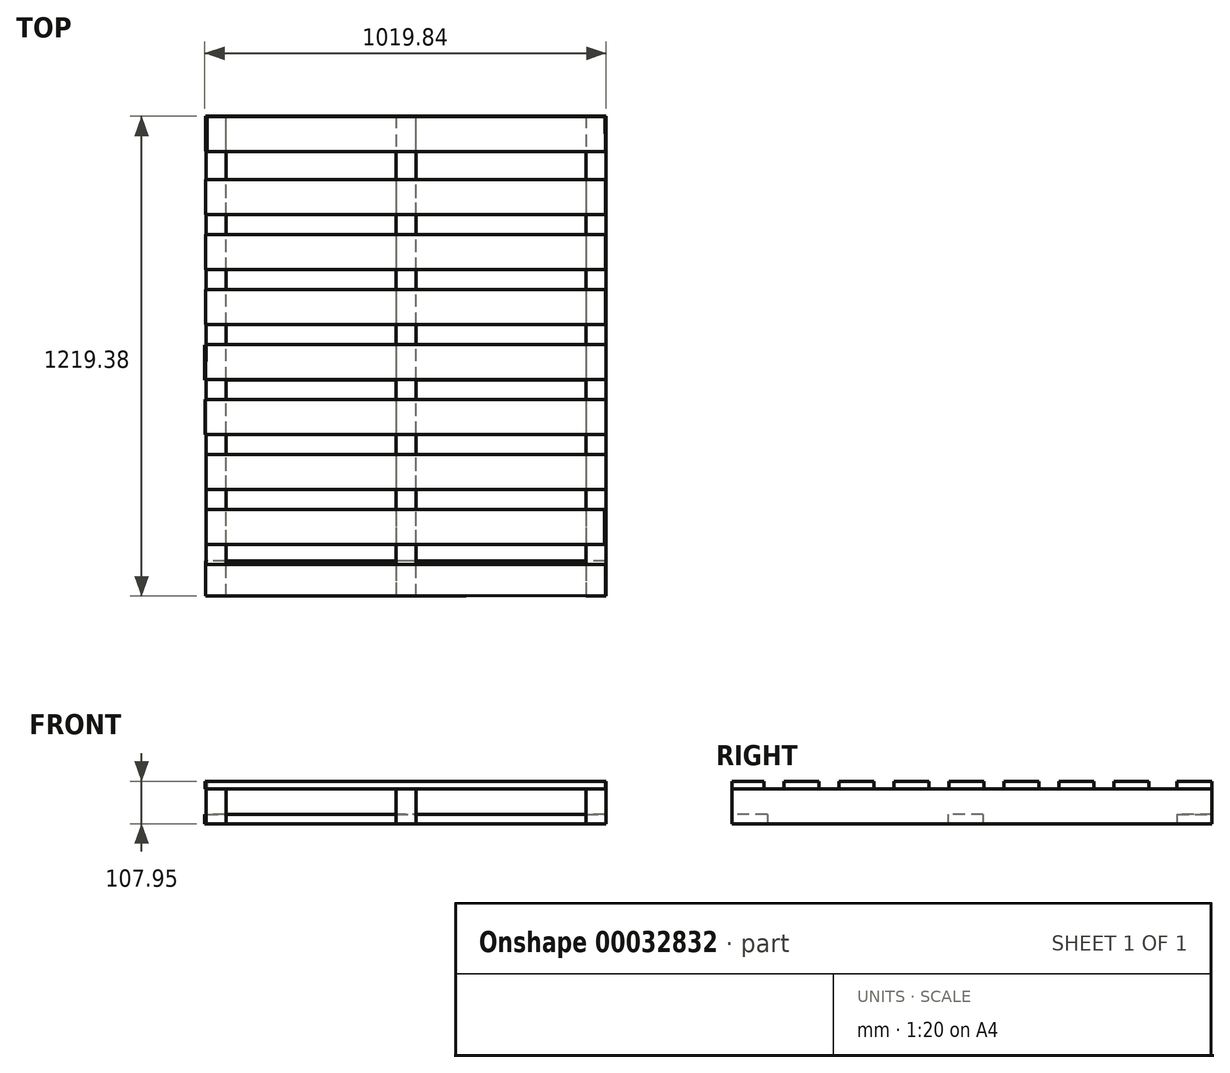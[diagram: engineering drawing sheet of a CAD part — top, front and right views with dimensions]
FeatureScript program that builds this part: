
annotation { "Feature Type Name" : "Feature", "Feature Type Description" : "" }
export const myFeature = defineFeature(function(context is Context, id is Id, definition is map)
    precondition{}
    {
        {
            var Q0;
            Q0=qCreatedBy(makeId("Top.planeOp"),FACE);
            var sketch = newSketch(context, id + "F0", { "sketchPlane" : qUnion([Q0])});
            skLineSegment(sketch, "E0", {"start": v(-409.62, 972.65) * mm, "end": v(-409.62, -246.55) * mm});
            skLineSegment(sketch, "E1", {"start": v(-409.62, -246.55) * mm, "end": v(-358.82, -246.55) * mm});
            skLineSegment(sketch, "E2", {"start": v(-358.82, -246.55) * mm, "end": v(-358.82, 972.65) * mm});
            skLineSegment(sketch, "E3", {"start": v(-358.82, 972.65) * mm, "end": v(-409.62, 972.65) * mm});
            skLineSegment(sketch, "E4", {"start": v(72.98, 972.65) * mm, "end": v(72.98, -246.55) * mm});
            skLineSegment(sketch, "E5", {"start": v(72.98, -246.55) * mm, "end": v(123.78, -246.55) * mm});
            skLineSegment(sketch, "E6", {"start": v(123.78, -246.55) * mm, "end": v(123.78, 972.65) * mm});
            skLineSegment(sketch, "E7", {"start": v(123.78, 972.65) * mm, "end": v(72.98, 972.65) * mm});
            skLineSegment(sketch, "E8", {"start": v(555.58, 972.65) * mm, "end": v(555.58, -246.55) * mm});
            skLineSegment(sketch, "E9", {"start": v(555.58, -246.55) * mm, "end": v(606.38, -246.55) * mm});
            skLineSegment(sketch, "E10", {"start": v(606.38, -246.55) * mm, "end": v(606.38, 972.65) * mm});
            skLineSegment(sketch, "E11", {"start": v(606.38, 972.65) * mm, "end": v(555.58, 972.65) * mm});
            skSolve(sketch);
        }
        {
            var Q0;
            Q0=makeQuery(id+"F0.imprint","IMPRINT",FACE,{"disambiguationData":[TD([[makeQuery(id+"F0.imprint","IMPRINT",EDGE,{"derivedFrom":sQuery(id+"F0.wireOp",EDGE,"E0")}),1.0]])]});
            var Q1;
            Q1=makeQuery(id+"F0.imprint","IMPRINT",FACE,{"disambiguationData":[TD([[makeQuery(id+"F0.imprint","IMPRINT",EDGE,{"derivedFrom":sQuery(id+"F0.wireOp",EDGE,"E4")}),1.0]])]});
            var Q2;
            Q2=makeQuery(id+"F0.imprint","IMPRINT",FACE,{"disambiguationData":[TD([[makeQuery(id+"F0.imprint","IMPRINT",EDGE,{"derivedFrom":sQuery(id+"F0.wireOp",EDGE,"E8")}),1.0]])]});
            extrude(context, id + "F1", {"entities" : qUnion([Q0, Q1, Q2]), "depth" : 88.9 * mm});
        }
        {
            var Q0;
            Q0=makeQuery(id+"F1.opExtrude","CAP_FACE",FACE,{"disambiguationData":[OSD([sQuery(id+"F0.wireOp",EDGE,"E4"),sQuery(id+"F0.wireOp",EDGE,"E5"),sQuery(id+"F0.wireOp",EDGE,"E6"),sQuery(id+"F0.wireOp",EDGE,"E7")])],"isStart":false});
            var sketch = newSketch(context, id + "F2", { "sketchPlane" : qUnion([Q0])});
            skLineSegment(sketch, "E12", {"start": v(-410.98, 812.34) * mm, "end": v(604.56, 812.34) * mm});
            skLineSegment(sketch, "E13", {"start": v(604.56, 812.34) * mm, "end": v(604.56, 723.44) * mm});
            skLineSegment(sketch, "E14", {"start": v(604.56, 723.44) * mm, "end": v(-410.98, 723.44) * mm});
            skLineSegment(sketch, "E15", {"start": v(-410.98, 723.44) * mm, "end": v(-410.98, 812.34) * mm});
            skLineSegment(sketch, "E16", {"start": v(-410.98, 672.64) * mm, "end": v(604.56, 672.64) * mm});
            skLineSegment(sketch, "E17", {"start": v(604.56, 672.64) * mm, "end": v(604.56, 583.74) * mm});
            skLineSegment(sketch, "E18", {"start": v(604.56, 583.74) * mm, "end": v(-410.98, 583.74) * mm});
            skLineSegment(sketch, "E19", {"start": v(-410.98, 583.74) * mm, "end": v(-410.98, 672.64) * mm});
            skLineSegment(sketch, "E20", {"start": v(-410.98, 532.94) * mm, "end": v(604.56, 532.94) * mm});
            skLineSegment(sketch, "E21", {"start": v(604.56, 532.94) * mm, "end": v(604.56, 444.04) * mm});
            skLineSegment(sketch, "E22", {"start": v(604.56, 444.04) * mm, "end": v(-410.98, 444.04) * mm});
            skLineSegment(sketch, "E23", {"start": v(-410.98, 444.04) * mm, "end": v(-410.98, 532.94) * mm});
            skLineSegment(sketch, "E24", {"start": v(-409.91, 393.24) * mm, "end": v(605.66, 393.24) * mm});
            skLineSegment(sketch, "E25", {"start": v(605.66, 393.24) * mm, "end": v(605.66, 304.34) * mm});
            skLineSegment(sketch, "E26", {"start": v(605.66, 304.34) * mm, "end": v(-410.98, 304.34) * mm});
            skLineSegment(sketch, "E27", {"start": v(-410.98, 304.34) * mm, "end": v(-409.91, 393.24) * mm});
            skLineSegment(sketch, "E28", {"start": v(-412.98, 253.54) * mm, "end": v(605.66, 253.54) * mm});
            skLineSegment(sketch, "E29", {"start": v(605.66, 253.54) * mm, "end": v(605.66, 164.64) * mm});
            skLineSegment(sketch, "E30", {"start": v(605.66, 164.64) * mm, "end": v(-412.98, 164.64) * mm});
            skLineSegment(sketch, "E31", {"start": v(-412.98, 164.64) * mm, "end": v(-412.98, 253.54) * mm});
            skLineSegment(sketch, "E32", {"start": v(-410.34, 113.84) * mm, "end": v(605.66, 113.84) * mm});
            skLineSegment(sketch, "E33", {"start": v(605.66, 113.84) * mm, "end": v(605.66, 24.94) * mm});
            skLineSegment(sketch, "E34", {"start": v(605.66, 24.94) * mm, "end": v(-410.34, 24.94) * mm});
            skLineSegment(sketch, "E35", {"start": v(-410.34, 24.94) * mm, "end": v(-410.34, 113.84) * mm});
            skLineSegment(sketch, "E36", {"start": v(-410.34, -25.86) * mm, "end": v(602.28, -25.86) * mm});
            skLineSegment(sketch, "E37", {"start": v(602.28, -25.86) * mm, "end": v(602.28, -114.76) * mm});
            skLineSegment(sketch, "E38", {"start": v(602.28, -114.76) * mm, "end": v(-410.34, -114.76) * mm});
            skLineSegment(sketch, "E39", {"start": v(-410.34, -114.76) * mm, "end": v(-410.34, -25.86) * mm});
            skLineSegment(sketch, "E40", {"start": v(-410.69, -245.09) * mm, "end": v(604.77, -246.55) * mm});
            skLineSegment(sketch, "E41", {"start": v(604.77, -246.55) * mm, "end": v(604.77, -165.56) * mm});
            skLineSegment(sketch, "E42", {"start": v(604.77, -165.56) * mm, "end": v(-410.69, -165.56) * mm});
            skLineSegment(sketch, "E43", {"start": v(-410.69, -165.56) * mm, "end": v(-410.69, -245.09) * mm});
            skLineSegment(sketch, "E44", {"start": v(604.77, 883.24) * mm, "end": v(604.53, 883.24) * mm});
            skLineSegment(sketch, "E45", {"start": v(-407.36, 972.14) * mm, "end": v(603.42, 972.14) * mm});
            skLineSegment(sketch, "E46", {"start": v(603.42, 972.14) * mm, "end": v(604.77, 883.24) * mm});
            skLineSegment(sketch, "E47", {"start": v(-407.36, 972.14) * mm, "end": v(-407.36, 883.24) * mm});
            skLineSegment(sketch, "E48", {"start": v(-407.36, 883.24) * mm, "end": v(604.77, 883.24) * mm});
            skSolve(sketch);
        }
        {
            var Q0;
            Q0 = qSketchRegion(id + "F2", true);
            extrude(context, id + "F3", {"entities" : qUnion([Q0]), "depth" : 19.05 * mm});
        }
        {
            var Q0;
            Q0=qCreatedBy(makeId("Top.planeOp"),FACE);
            var sketch = newSketch(context, id + "F4", { "sketchPlane" : qUnion([Q0])});
            skLineSegment(sketch, "E49", {"start": v(-411.07, -246.04) * mm, "end": v(604.47, -246.04) * mm});
            skLineSegment(sketch, "E50", {"start": v(604.47, -246.04) * mm, "end": v(604.47, -157.14) * mm});
            skLineSegment(sketch, "E51", {"start": v(604.47, -157.14) * mm, "end": v(-411.07, -157.14) * mm});
            skLineSegment(sketch, "E52", {"start": v(-411.07, -157.14) * mm, "end": v(-411.07, -246.04) * mm});
            skLineSegment(sketch, "E53", {"start": v(-411.07, 883.93) * mm, "end": v(-411.07, 972.83) * mm});
            skLineSegment(sketch, "E54", {"start": v(-411.07, 972.83) * mm, "end": v(604.47, 972.83) * mm});
            skLineSegment(sketch, "E55", {"start": v(604.47, 972.83) * mm, "end": v(604.47, 883.93) * mm});
            skLineSegment(sketch, "E56", {"start": v(604.47, 883.93) * mm, "end": v(-411.07, 883.93) * mm});
            skLineSegment(sketch, "E57", {"start": v(-413.46, 302.26) * mm, "end": v(604.47, 302.26) * mm});
            skLineSegment(sketch, "E58", {"start": v(604.47, 302.26) * mm, "end": v(604.47, 391.16) * mm});
            skLineSegment(sketch, "E59", {"start": v(604.47, 391.16) * mm, "end": v(-413.46, 391.16) * mm});
            skLineSegment(sketch, "E60", {"start": v(-413.46, 391.16) * mm, "end": v(-413.46, 302.26) * mm});
            skLineSegment(sketch, "E61", {"start": v(-411.07, -246.04) * mm, "end": v(-413.46, 302.26) * mm});
            skSolve(sketch);
        }
        {
            var Q0;
            Q0 = qSketchRegion(id + "F4", true);
            extrude(context, id + "F5", {"entities" : qUnion([Q0]), "depth" : 24.13 * mm});
        }
    });
